# Revit family: QF_BPRO_TTW 20-115 DZG_573736
name_source: partatom
category: Sonderausstattung
revit_build: Autodesk Revit 2018 (Build: 20190510_1515(x64)
units: mm (PartAtom-declared; Revit-internal decimal feet)

## family parameters
Arbeitsebenenbasiert = Nein
Beim Laden mit Abzugskörper schneiden = Nein
Bemaßung runder Anschluss = Durchmesser verwenden
Gemeinsam genutzt = Nein
Immer vertikal = Ja
Raumberechnungspunkt = Ja
Teiletyp = Normal

## types (1)
- TTW 20-115 DZG
    Artikel Nummer = 573736
    Beschreibung = Tablett-Transportwagen,  doppelwandig, isoliert
2 Schrankräume

Kapazität: 20 Gastronorm-Tabletts
Einschubart: Längseinschub
Sickenabstand: 115 mm
    Beschreibung durch Hersteller analog Leistungsverzeichniskurztext = Tablett-Transportwagen
in doppelwandiger Ausführung
TTW 20-115 DZG

Abmessungen

Länge:	 1032	mm
Breite:	   783	mm
Höhe:	 1636	mm


Ausführung

Aufbau

Der Wagenkorpus ist allseitig geschlossen und komplett in CNS 18/10 ausgeführt. Die Oberfläche ist mikroliert. Das gekantete Bodenblech ist an der Unterseite mit Längsprofilen verstärkt. Die Türen sind doppelwandig und mit Polystyrol Hartschaumplatten isoliert. Innen- und Außenkorpus sind vertikal mit Kunststoffprofilen verbunden und thermisch getrennt.
Seitenwände und Mittelwand im Schrankfach sind zur Tablett-Ablage mit nahtlos tiefgezogenen Auflagesicken im Abstand von 115 mm ausgeführt. Über den Tablett-Auflagen befinden sich in einem Abstand von 7 mm zwei nahtlos tiefgezogene Kippsicherungen, die beim herausziehen der Tabletts ein ungewolltes Abkippen verhindern. Die Auflagesicken haben eine Breite von 11,5 mm zur sicheren Aufnahme von Gastronorm-Tabletts (530 x 325 mm). Die selbsttragende Bauweise gewährleistet einen Einsatz im Außer-Haus- und im Hausbetrieb.
Die doppelwandigen Flügeltüren sind um 270° zu öffnen und mithilfe eines federbelasteten Kunststoff-Formteils am Boden des Tablett-Transportwagens sicher arretierbar. Die im geöffneten Zustand arretierten Türen befinden sich innerhalb des Stoßschutzes, um Beschädigungen zu vermeiden. Zusätzlich verfügen die Türen über ein umlaufendes, herausnehmbares Silikondichtungsprofil.
Der vertikal mittig an den Türen angebrachte Türverschluss ist selbst schließend und mit integrierter Transportsicherung ausgeführt. Die robusten Türscharniere sind geschweißt und stoßgesichert, da sie innerhalb des Stoßschutzes liegen. 





Einsatz/Ergonomie

Der Tablett-Transportwagen ist zum Transport von portionierten Speisen auf Tabletts konzipiert.
Er ist mit einem umlaufenden, robusten Stoßschutz ausgestattet, der den Wagen vor Beschädigungen schützt. An den beiden Stirnseiten befinden sich jeweils zwei senkrechte, ergonomisch angeordnete Schiebegriffe. Die Schiebegriffe befinden sich innerhalb des Stoßschutzes um ein Quetschen der Hände beim Durchfahren von Türen und schmalen Gängen zu vermeiden. Die Schiebegriffe sind auch bei geöffneter Tür erreichbar.
Der Tablett-Transportwagen ist fahrbar mittels 2 Bockrollen und 2 Lenkrollen mit Feststeller, Ø 160 mm, Gehäuse stahlverzinkt.



Besonderheit

•	Türverschlüsse selbstschließend mit integrierter Transportsicherung
•	Türen mit umlaufendem, herausnehmbarem Dichtungsprofil
•	Innen- und Außenkorpus vertikal mit Kunststoffprofilen verbunden und thermisch getrennt



Technische Daten

Werkstoff:	Chromnickelstahl 18/10, Werkstoff-Nr. 1.4301
	Polyethylen (PE)
Isoliermaterial
Türen und Wände:	Polystyrol Hartschaumplatten (30 mm)
Gewicht:	                        ca. 118 kg
Kapazität:	20 Gastronorm-Tabletts (530x325mm)
Einschubart:	Längseinschub
Abstand der 
Auflagesicken:	115 mm
Abstand 
Kippsicherung / Sicken:	7 mm
Anzahl Schrankräume:	2
Anzahl Flügeltüren:	                        2
Innenraumausführung:	Hygieneausführung HS, 
	gem. DIN 18865-9

Zubehör/ Optionen

•	Sickenabstand 105 mm (Breite Auflagesicken: 14 mm)
•	Umlaufender Stoßschutz gefräst
•	Zusätzlicher Stoßschutz am Dach
•	Galerie umlaufend, auf Gehrung geschweißt
•	Zugdeichsel und Kupplung
•	Antistatikband
•	Rollendurchmesser 200 mm
•	CNS-Rollen mit Elastikbereifung
•	Rollenanordnung D mit Zentralfeststeller




Fabrikat:

Hersteller:	B.PRO
Typ:	                        TTW 20-115 DZG
Best.-Nr.:	                         573736
    Beschreibung durch Hersteller analog Leistungsverzeichnislangtext = Tablett-Transportwagen
in doppelwandiger Ausführung
TTW 20-115 DZG

Abmessungen

Länge:	 1032	mm
Breite:	   783	mm
Höhe:	 1636	mm


Ausführung

Aufbau

Der Wagenkorpus ist allseitig geschlossen und komplett in CNS 18/10 ausgeführt. Die Oberfläche ist mikroliert. Das gekantete Bodenblech ist an der Unterseite mit Längsprofilen verstärkt. Die Türen sind doppelwandig und mit Polystyrol Hartschaumplatten isoliert. Innen- und Außenkorpus sind vertikal mit Kunststoffprofilen verbunden und thermisch getrennt.
Seitenwände und Mittelwand im Schrankfach sind zur Tablett-Ablage mit nahtlos tiefgezogenen Auflagesicken im Abstand von 115 mm ausgeführt. Über den Tablett-Auflagen befinden sich in einem Abstand von 7 mm zwei nahtlos tiefgezogene Kippsicherungen, die beim herausziehen der Tabletts ein ungewolltes Abkippen verhindern. Die Auflagesicken haben eine Breite von 11,5 mm zur sicheren Aufnahme von Gastronorm-Tabletts (530 x 325 mm). Die selbsttragende Bauweise gewährleistet einen Einsatz im Außer-Haus- und im Hausbetrieb.
Die doppelwandigen Flügeltüren sind um 270° zu öffnen und mithilfe eines federbelasteten Kunststoff-Formteils am Boden des Tablett-Transportwagens sicher arretierbar. Die im geöffneten Zustand arretierten Türen befinden sich innerhalb des Stoßschutzes, um Beschädigungen zu vermeiden. Zusätzlich verfügen die Türen über ein umlaufendes, herausnehmbares Silikondichtungsprofil.
Der vertikal mittig an den Türen angebrachte Türverschluss ist selbst schließend und mit integrierter Transportsicherung ausgeführt. Die robusten Türscharniere sind geschweißt und stoßgesichert, da sie innerhalb des Stoßschutzes liegen. 





Einsatz/Ergonomie

Der Tablett-Transportwagen ist zum Transport von portionierten Speisen auf Tabletts konzipiert.
Er ist mit einem umlaufenden, robusten Stoßschutz ausgestattet, der den Wagen vor Beschädigungen schützt. An den beiden Stirnseiten befinden sich jeweils zwei senkrechte, ergonomisch angeordnete Schiebegriffe. Die Schiebegriffe befinden sich innerhalb des Stoßschutzes um ein Quetschen der Hände beim Durchfahren von Türen und schmalen Gängen zu vermeiden. Die Schiebegriffe sind auch bei geöffneter Tür erreichbar.
Der Tablett-Transportwagen ist fahrbar mittels 2 Bockrollen und 2 Lenkrollen mit Feststeller, Ø 160 mm, Gehäuse stahlverzinkt.



Besonderheit

•	Türverschlüsse selbstschließend mit integrierter Transportsicherung
•	Türen mit umlaufendem, herausnehmbarem Dichtungsprofil
•	Innen- und Außenkorpus vertikal mit Kunststoffprofilen verbunden und thermisch getrennt



Technische Daten

Werkstoff:	Chromnickelstahl 18/10, Werkstoff-Nr. 1.4301
	Polyethylen (PE)
Isoliermaterial
Türen und Wände:	Polystyrol Hartschaumplatten (30 mm)
Gewicht:	                        ca. 118 kg
Kapazität:	20 Gastronorm-Tabletts (530x325mm)
Einschubart:	Längseinschub
Abstand der 
Auflagesicken:	115 mm
Abstand 
Kippsicherung / Sicken:	7 mm
Anzahl Schrankräume:	2
Anzahl Flügeltüren:	                        2
Innenraumausführung:	Hygieneausführung HS, 
	gem. DIN 18865-9

Zubehör/ Optionen

•	Sickenabstand 105 mm (Breite Auflagesicken: 14 mm)
•	Umlaufender Stoßschutz gefräst
•	Zusätzlicher Stoßschutz am Dach
•	Galerie umlaufend, auf Gehrung geschweißt
•	Zugdeichsel und Kupplung
•	Antistatikband
•	Rollendurchmesser 200 mm
•	CNS-Rollen mit Elastikbereifung
•	Rollenanordnung D mit Zentralfeststeller




Fabrikat:

Hersteller:	B.PRO
Typ:	                        TTW 20-115 DZG
Best.-Nr.:	                         573736
    Gerätegewicht Netto = 118.00 kg
    Großküchengerätezuordnung = Ja
    Hersteller = B.PRO GmbH
    Höhe = 1636 mm
    Höhe Korpus = 1375 mm
    Internetadresse Gerätehersteller = https://www.bpro-solutions.com
    Internetadresse für Ersatzteilliste = https://www.bpro-solutions.com
    Kosten = 4556 $
    Länge Gerätebreite = 1032 mm  [stored 3.38583 ft]
    Länge Korpus = 777 mm
    Material = QF_Metal-Stainless-Steel_general
    Material_Stoßschutz = QF_Rubber-Black-Matt
    Modell = TTW 20-115 DZG
    Sockelhöhe = 195 mm  [stored 0.639764 ft]
    Tiefe = 783 mm  [stored 2.5689 ft]
    Tiefe Korpus = 645 mm  [stored 2.11614 ft]
    Typenkommentare = Tablett-Transportwagen, doppelwandig, isoliert
    URL = https://www.bpro-solutions.com
    Warnhinweise = Verletzungsgefahr:

 - Hände können beim Arretieren der Gerätetür eingeklemmt und dabei verletzt werden.
    > Hand beim Arretieren nicht zwischen die Gerätetür und das Gerät bringen oder halten.
    > Gerätetür vorsichtig (ohne Schwung) öffnen und arreitieren.

 - Wenn nur im oberen Bereich des Geräts Tabletts eingebracht werden, verlagert sich der Schwerpunkt nach oben, und es besteht die Gefahr, dass das Gerät kippt. Ein kippendes Gerät kann schwere Verletzungen verursachen.
    > Das Gerät stets von unten nach oben beschicken.
    > Bei einer Teilbestückung nur den unteren Geräteraum beschicken.

 - Das Gerät kann beim Befahren einer schrägen Fläche umkippen.
    > Das Gerät niemals über eine Fläche mit einer Neigung > 10° fahren.
    > Das Gerät stets von unten nach oben beschicken.
    > Bei einer Teilbestückung nur den unteren Geräteraum beschicken.

Ausführliche Gefahrenhinweise entnehmen Sie der Betriebsanleitung.
    Zubehör = Nein

note: [stored X ft] marks values corroborated as IEEE doubles in the binary element streams (Revit-internal decimal feet)
